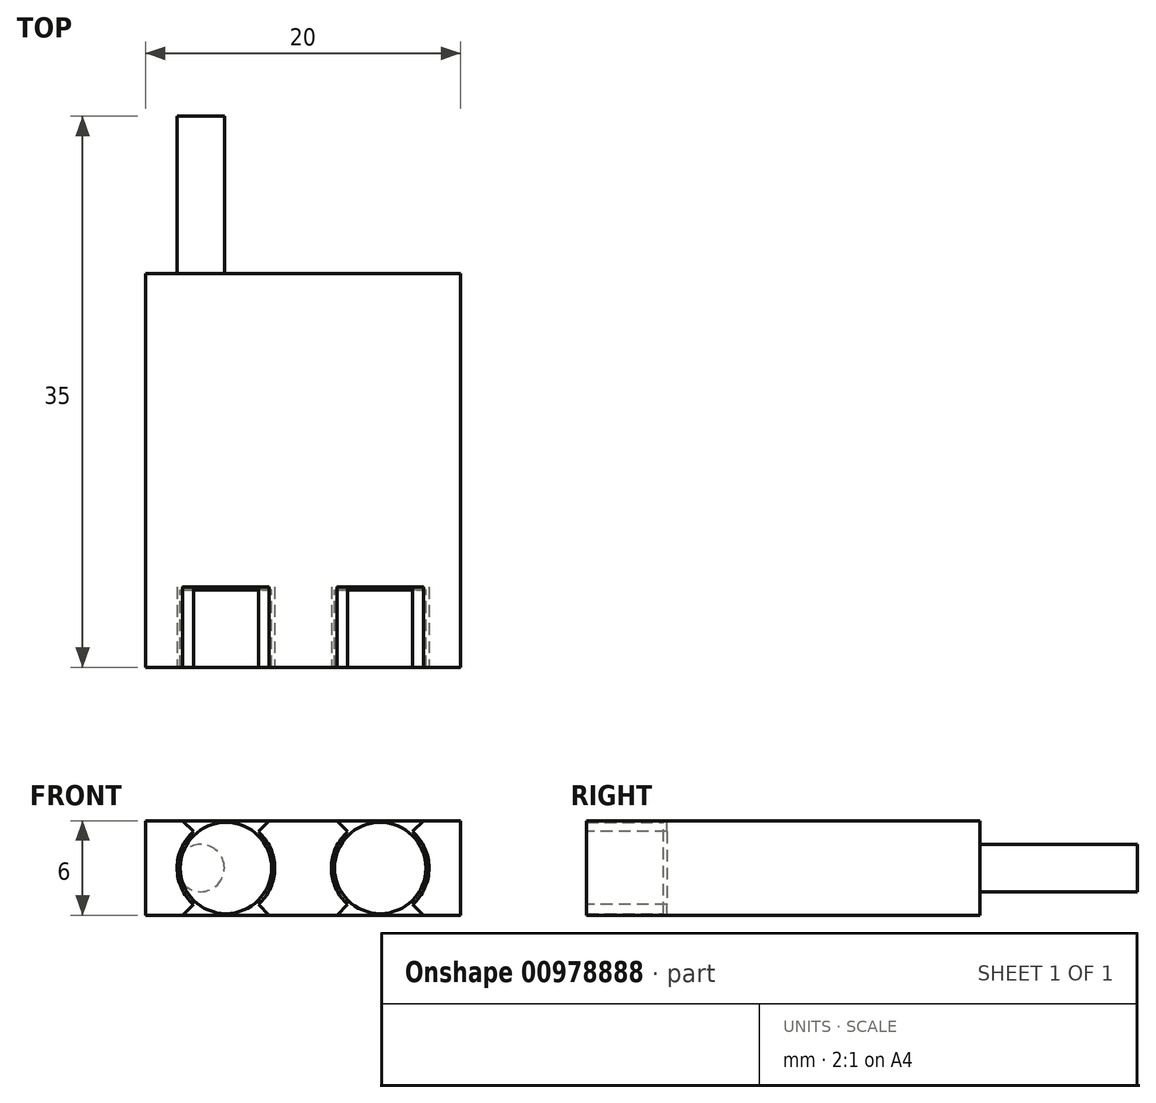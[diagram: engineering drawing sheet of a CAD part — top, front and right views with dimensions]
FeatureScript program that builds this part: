
annotation { "Feature Type Name" : "Feature", "Feature Type Description" : "" }
export const myFeature = defineFeature(function(context is Context, id is Id, definition is map)
    precondition{}
    {
        {
            var Q0;
            Q0=qCreatedBy(makeId("Front.planeOp"),FACE);
            var sketch = newSketch(context, id + "F0", { "sketchPlane" : qUnion([Q0])});
            skLineSegment(sketch, "E0.bottom", {"start": v(-10, 3) * mm, "end": v(10, 3) * mm});
            skLineSegment(sketch, "E0.top", {"start": v(-10, -3) * mm, "end": v(10, -3) * mm});
            skLineSegment(sketch, "E0.left", {"start": v(-10, 3) * mm, "end": v(-10, -3) * mm});
            skLineSegment(sketch, "E0.right", {"start": v(10, 3) * mm, "end": v(10, -3) * mm});
            skPoint(sketch, "E0.middle", {"position": v(0, 0) * mm});
            skPoint(sketch, "E1.visualSharp", {"position": v(-10, 3) * mm});
            skPoint(sketch, "E2.visualSharp", {"position": v(10, 3) * mm});
            skPoint(sketch, "E3.visualSharp", {"position": v(10, -3) * mm});
            skPoint(sketch, "E4.visualSharp", {"position": v(-10, -3) * mm});
            skSolve(sketch);
        }
        {
            var Q0;
            Q0=makeQuery(id+"F0.imprint","IMPRINT",FACE,{"disambiguationData":[TD([[makeQuery(id+"F0.imprint","IMPRINT",EDGE,{"derivedFrom":sQuery(id+"F0.wireOp",EDGE,"E0.bottom")}),-1.0]])]});
            extrude(context, id + "F1", {"entities" : qUnion([Q0]), "depth" : 35 * mm, "offsetDistance" : 25 * mm});
        }
        {
            var Q0;
            Q0=makeQuery(id+"F1.opExtrude","CAP_FACE",FACE,{"disambiguationData":[OSD([sQuery(id+"F0.wireOp",EDGE,"E0.bottom"),sQuery(id+"F0.wireOp",EDGE,"E0.top"),sQuery(id+"F0.wireOp",EDGE,"E0.left"),sQuery(id+"F0.wireOp",EDGE,"E0.right"),sQuery(id+"F0.wireOp",EDGE,"E1.filletArc"),sQuery(id+"F0.wireOp",EDGE,"E2.filletArc"),sQuery(id+"F0.wireOp",EDGE,"E3.filletArc"),sQuery(id+"F0.wireOp",EDGE,"E4.filletArc")])],"isStart":false});
            var sketch = newSketch(context, id + "F2", { "sketchPlane" : qUnion([Q0])});
            skArc(sketch, "E5", {"start": v(-6.65, 2.56) * mm, "mid": v(-8, 0) * mm, "end": v(-6.65, -2.56) * mm});
            skArc(sketch, "E6", {"start": v(6.65, -2.56) * mm, "mid": v(8, 0) * mm, "end": v(6.65, 2.56) * mm});
            skLineSegment(sketch, "E7", {"start": v(-6.65, 2.56) * mm, "end": v(-6.65, 3.1) * mm});
            skLineSegment(sketch, "E8", {"start": v(-6.65, 3.1) * mm, "end": v(-3.15, 3.1) * mm});
            skLineSegment(sketch, "E9", {"start": v(6.65, 2.56) * mm, "end": v(6.65, 3.1) * mm});
            skLineSegment(sketch, "E10", {"start": v(-3.15, 2.56) * mm, "end": v(-3.15, 3.1) * mm});
            skLineSegment(sketch, "E11", {"start": v(3.15, 2.56) * mm, "end": v(3.15, 3.1) * mm});
            skLineSegment(sketch, "E12", {"start": v(-6.65, 2.56) * mm, "end": v(6.65, 2.56) * mm, "construction": true});
            skLineSegment(sketch, "E13", {"start": v(-4.9, 0) * mm, "end": v(4.9, 0) * mm, "construction": true});
            skLineSegment(sketch, "E14.MirrorCS", {"start": v(6.65, -2.56) * mm, "end": v(6.65, -3.1) * mm});
            skLineSegment(sketch, "E15.MirrorCS", {"start": v(-6.65, -3.1) * mm, "end": v(-3.15, -3.1) * mm});
            skLineSegment(sketch, "E16.MirrorCS", {"start": v(3.15, -2.56) * mm, "end": v(3.15, -3.1) * mm});
            skLineSegment(sketch, "E17.MirrorCS", {"start": v(-3.15, -2.56) * mm, "end": v(-3.15, -3.1) * mm});
            skLineSegment(sketch, "E18.MirrorCS", {"start": v(-6.65, -2.56) * mm, "end": v(-6.65, -3.1) * mm});
            skLineSegment(sketch, "E19.trimOffspring", {"start": v(3.15, 3.1) * mm, "end": v(6.65, 3.1) * mm});
            skArc(sketch, "E20.trimOffspring", {"start": v(-3.15, -2.56) * mm, "mid": v(-1.8, 0) * mm, "end": v(-3.15, 2.56) * mm});
            skLineSegment(sketch, "E21.trimOffspring", {"start": v(3.15, -3.1) * mm, "end": v(6.65, -3.1) * mm});
            skArc(sketch, "E22.trimOffspring", {"start": v(3.15, 2.56) * mm, "mid": v(1.8, 0) * mm, "end": v(3.15, -2.56) * mm});
            skSolve(sketch);
        }
        {
            var Q0;
            Q0 = qSketchRegion(id + "F2", true);
            extrude(context, id + "F3", {"entities" : qUnion([Q0]), "operationType" : NewBodyOperationType.REMOVE, "oppositeDirection" : true, "depth" : 5.1 * mm, "offsetDistance" : 25 * mm});
        }
        {
            var Q0;
            Q0=makeQuery(id+"F3.boolean.opBoolean","INTERSECT",EDGE,{"derivedFrom":[makeQuery(id+"F1.opExtrude","SWEPT_FACE",FACE,{"disambiguationData":[OSD([sQuery(id+"F0.wireOp",EDGE,"E0.bottom")])]}),makeQuery(id+"F3.opExtrude","SWEPT_FACE",FACE,{"disambiguationData":[OSD([sQuery(id+"F2.wireOp",EDGE,"E7")])]})]});
            var Q1;
            Q1=makeQuery(id+"F3.boolean.opBoolean","INTERSECT",EDGE,{"derivedFrom":[makeQuery(id+"F1.opExtrude","SWEPT_FACE",FACE,{"disambiguationData":[OSD([sQuery(id+"F0.wireOp",EDGE,"E0.bottom")])]}),makeQuery(id+"F3.opExtrude","SWEPT_FACE",FACE,{"disambiguationData":[OSD([sQuery(id+"F2.wireOp",EDGE,"E10")])]})]});
            var Q2;
            Q2=makeQuery(id+"F3.boolean.opBoolean","INTERSECT",EDGE,{"derivedFrom":[makeQuery(id+"F1.opExtrude","SWEPT_FACE",FACE,{"disambiguationData":[OSD([sQuery(id+"F0.wireOp",EDGE,"E0.bottom")])]}),makeQuery(id+"F3.opExtrude","SWEPT_FACE",FACE,{"disambiguationData":[OSD([sQuery(id+"F2.wireOp",EDGE,"E11")])]})]});
            var Q3;
            Q3=makeQuery(id+"F3.boolean.opBoolean","INTERSECT",EDGE,{"derivedFrom":[makeQuery(id+"F1.opExtrude","SWEPT_FACE",FACE,{"disambiguationData":[OSD([sQuery(id+"F0.wireOp",EDGE,"E0.bottom")])]}),makeQuery(id+"F3.opExtrude","SWEPT_FACE",FACE,{"disambiguationData":[OSD([sQuery(id+"F2.wireOp",EDGE,"E9")])]})]});
            var Q4;
            Q4=makeQuery(id+"F3.boolean.opBoolean","INTERSECT",EDGE,{"derivedFrom":[makeQuery(id+"F1.opExtrude","SWEPT_FACE",FACE,{"disambiguationData":[OSD([sQuery(id+"F0.wireOp",EDGE,"E0.top")])]}),makeQuery(id+"F3.opExtrude","SWEPT_FACE",FACE,{"disambiguationData":[OSD([sQuery(id+"F2.wireOp",EDGE,"E18.MirrorCS")])]})]});
            var Q5;
            Q5=makeQuery(id+"F3.boolean.opBoolean","INTERSECT",EDGE,{"derivedFrom":[makeQuery(id+"F1.opExtrude","SWEPT_FACE",FACE,{"disambiguationData":[OSD([sQuery(id+"F0.wireOp",EDGE,"E0.top")])]}),makeQuery(id+"F3.opExtrude","SWEPT_FACE",FACE,{"disambiguationData":[OSD([sQuery(id+"F2.wireOp",EDGE,"E17.MirrorCS")])]})]});
            var Q6;
            Q6=makeQuery(id+"F3.boolean.opBoolean","INTERSECT",EDGE,{"derivedFrom":[makeQuery(id+"F1.opExtrude","SWEPT_FACE",FACE,{"disambiguationData":[OSD([sQuery(id+"F0.wireOp",EDGE,"E0.top")])]}),makeQuery(id+"F3.opExtrude","SWEPT_FACE",FACE,{"disambiguationData":[OSD([sQuery(id+"F2.wireOp",EDGE,"E16.MirrorCS")])]})]});
            var Q7;
            Q7=makeQuery(id+"F3.boolean.opBoolean","INTERSECT",EDGE,{"derivedFrom":[makeQuery(id+"F1.opExtrude","SWEPT_FACE",FACE,{"disambiguationData":[OSD([sQuery(id+"F0.wireOp",EDGE,"E0.top")])]}),makeQuery(id+"F3.opExtrude","SWEPT_FACE",FACE,{"disambiguationData":[OSD([sQuery(id+"F2.wireOp",EDGE,"E14.MirrorCS")])]})]});
            chamfer(context, id + "F4", {"entities" : qUnion([Q0, Q1, Q2, Q3, Q4, Q5, Q6, Q7]), "chamferType" : ChamferType.OFFSET_ANGLE, "width" : 1 * mm, "oppositeDirection" : false, "angle" : 45 * degree, "tangentPropagation" : true});
        }
        {
            var Q0;
            Q0=makeQuery(id+"F1.opExtrude","CAP_FACE",FACE,{"disambiguationData":[OSD([sQuery(id+"F0.wireOp",EDGE,"E0.bottom"),sQuery(id+"F0.wireOp",EDGE,"E0.top"),sQuery(id+"F0.wireOp",EDGE,"E0.left"),sQuery(id+"F0.wireOp",EDGE,"E0.right"),sQuery(id+"F0.wireOp",EDGE,"E1.filletArc"),sQuery(id+"F0.wireOp",EDGE,"E2.filletArc"),sQuery(id+"F0.wireOp",EDGE,"E3.filletArc"),sQuery(id+"F0.wireOp",EDGE,"E4.filletArc")])],"isStart":true});
            var sketch = newSketch(context, id + "F5", { "sketchPlane" : qUnion([Q0])});
            skCircle(sketch, "E23", {"center": v(-6.5, 0) * mm, "radius": 1.5 * mm});
            skLineSegment(sketch, "E24", {"start": v(0, 3) * mm, "end": v(0, -3) * mm, "construction": true});
            skCircle(sketch, "E25.MirrorC", {"center": v(6.5, 0) * mm, "radius": 1.5 * mm});
            skSolve(sketch);
        }
        {
            var Q0;
            Q0=makeQuery(id+"F3.boolean.opBoolean","COPY",FACE,{"derivedFrom":makeQuery(id+"F3.opExtrude","CAP_FACE",FACE,{"disambiguationData":[OSD([sQuery(id+"F2.wireOp",EDGE,"E5"),sQuery(id+"F2.wireOp",EDGE,"E7"),sQuery(id+"F2.wireOp",EDGE,"E8"),sQuery(id+"F2.wireOp",EDGE,"E10"),sQuery(id+"F2.wireOp",EDGE,"E15.MirrorCS"),sQuery(id+"F2.wireOp",EDGE,"E17.MirrorCS"),sQuery(id+"F2.wireOp",EDGE,"E18.MirrorCS"),sQuery(id+"F2.wireOp",EDGE,"E20.trimOffspring")])],"isStart":false})});
            cPlane(context, id + "F6", {"entities" : qUnion([Q0]), "cplaneType" : CPlaneType.OFFSET, "offset" : .2 * mm, "width" : 150 * mm, "height" : 150 * mm});
        }
        {
            var Q0;
            Q0=qCreatedBy(id+"F6.planeOp",FACE);
            var sketch = newSketch(context, id + "F7", { "sketchPlane" : qUnion([Q0])});
            skCircle(sketch, "E26", {"center": v(-4.9, 0) * mm, "radius": 2.9 * mm});
            skCircle(sketch, "E27", {"center": v(4.9, 0) * mm, "radius": 2.9 * mm});
            skSolve(sketch);
        }
        {
            var Q0;
            Q0=makeQuery(id+"F7.imprint","IMPRINT",FACE,{"disambiguationData":[TD([[makeQuery(id+"F7.imprint","IMPRINT",EDGE,{"derivedFrom":sQuery(id+"F7.wireOp",EDGE,"E26")}),1.0]])]});
            var Q1;
            Q1=makeQuery(id+"F7.imprint","IMPRINT",FACE,{"disambiguationData":[TD([[makeQuery(id+"F7.imprint","IMPRINT",EDGE,{"derivedFrom":sQuery(id+"F7.wireOp",EDGE,"E27")}),1.0]])]});
            extrude(context, id + "F8", {"entities" : qUnion([Q0, Q1]), "depth" : 4.9 * mm, "offsetDistance" : 25 * mm});
        }
        {
            var Q0;
            Q0=makeQuery(id+"F5.imprint","IMPRINT",FACE,{"disambiguationData":[TD([[makeQuery(id+"F5.imprint","IMPRINT",EDGE,{"derivedFrom":sQuery(id+"F5.wireOp",EDGE,"E23")}),1.0]])]});
            var Q1;
            Q1=makeQuery(id+"F5.imprint","IMPRINT",FACE,{"disambiguationData":[TD([[makeQuery(id+"F5.imprint","IMPRINT",EDGE,{"derivedFrom":sQuery(id+"F5.wireOp",EDGE,"E25.MirrorC")}),-1.0]])]});
            extrude(context, id + "F9", {"entities" : qUnion([Q0, Q1]), "operationType" : NewBodyOperationType.REMOVE, "oppositeDirection" : true, "depth" : 10 * mm, "offsetDistance" : 25 * mm});
        }
    });
